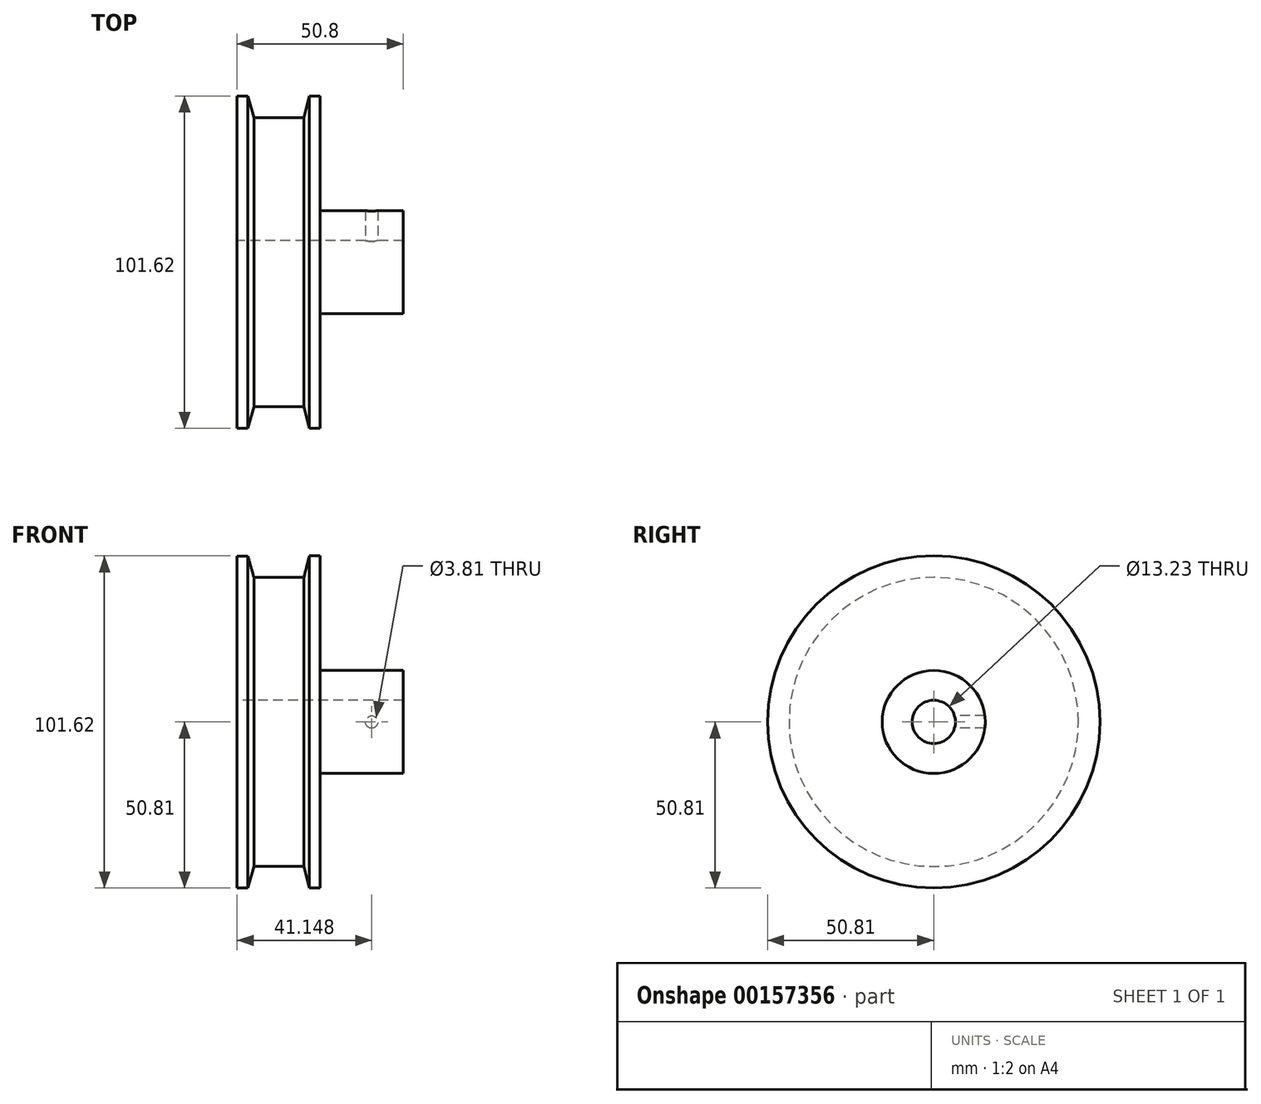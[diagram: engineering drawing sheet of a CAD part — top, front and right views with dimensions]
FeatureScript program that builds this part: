
annotation { "Feature Type Name" : "Feature", "Feature Type Description" : "" }
export const myFeature = defineFeature(function(context is Context, id is Id, definition is map)
    precondition{}
    {
        {
            var Q0;
            Q0=qCreatedBy(makeId("Front.planeOp"),FACE);
            var sketch = newSketch(context, id + "F0", { "sketchPlane" : qUnion([Q0])});
            skLineSegment(sketch, "E0", {"start": v(0, 0) * mm, "end": v(100.45, 0) * mm, "construction": true});
            skLineSegment(sketch, "E1", {"start": v(0, 6.61) * mm, "end": v(50.8, 6.61) * mm});
            skLineSegment(sketch, "E2", {"start": v(50.8, 6.61) * mm, "end": v(50.8, 15.76) * mm});
            skLineSegment(sketch, "E3", {"start": v(50.8, 15.76) * mm, "end": v(25.4, 15.76) * mm});
            skLineSegment(sketch, "E4", {"start": v(25.4, 15.76) * mm, "end": v(25.4, 50.8) * mm});
            skLineSegment(sketch, "E5", {"start": v(25.4, 50.8) * mm, "end": v(22.1, 50.8) * mm});
            skLineSegment(sketch, "E6", {"start": v(22.1, 50.8) * mm, "end": v(20.43, 44.22) * mm});
            skLineSegment(sketch, "E7", {"start": v(20.43, 44.22) * mm, "end": v(5.15, 44.22) * mm});
            skLineSegment(sketch, "E8", {"start": v(5.15, 44.22) * mm, "end": v(3.3, 50.76) * mm});
            skLineSegment(sketch, "E9", {"start": v(3.3, 50.76) * mm, "end": v(0, 50.76) * mm});
            skLineSegment(sketch, "E10", {"start": v(0, 50.76) * mm, "end": v(0, 6.61) * mm});
            skSolve(sketch);
        }
        {
            var Q0;
            Q0 = qSketchRegion(id + "F0", true);
            var Q1;
            Q1=sQuery(id+"F0.wireOp",EDGE,"E0");
            revolve(context, id + "F1", {"entities" : qUnion([Q0]), "axis" : qUnion([Q1]), "revolveType" : RevolveType.FULL});
        }
        {
            var Q0;
            Q0=qCreatedBy(makeId("Front.planeOp"),FACE);
            var sketch = newSketch(context, id + "F2", { "sketchPlane" : qUnion([Q0])});
            skCircle(sketch, "E11", {"center": v(41.15, 0) * mm, "radius": 1.9 * mm});
            skSolve(sketch);
        }
        {
            var Q0;
            Q0 = qSketchRegion(id + "F2", true);
            extrude(context, id + "F3", {"entities" : qUnion([Q0]), "operationType" : NewBodyOperationType.REMOVE, "oppositeDirection" : true, "depth" : 25.4 * mm});
        }
    });
